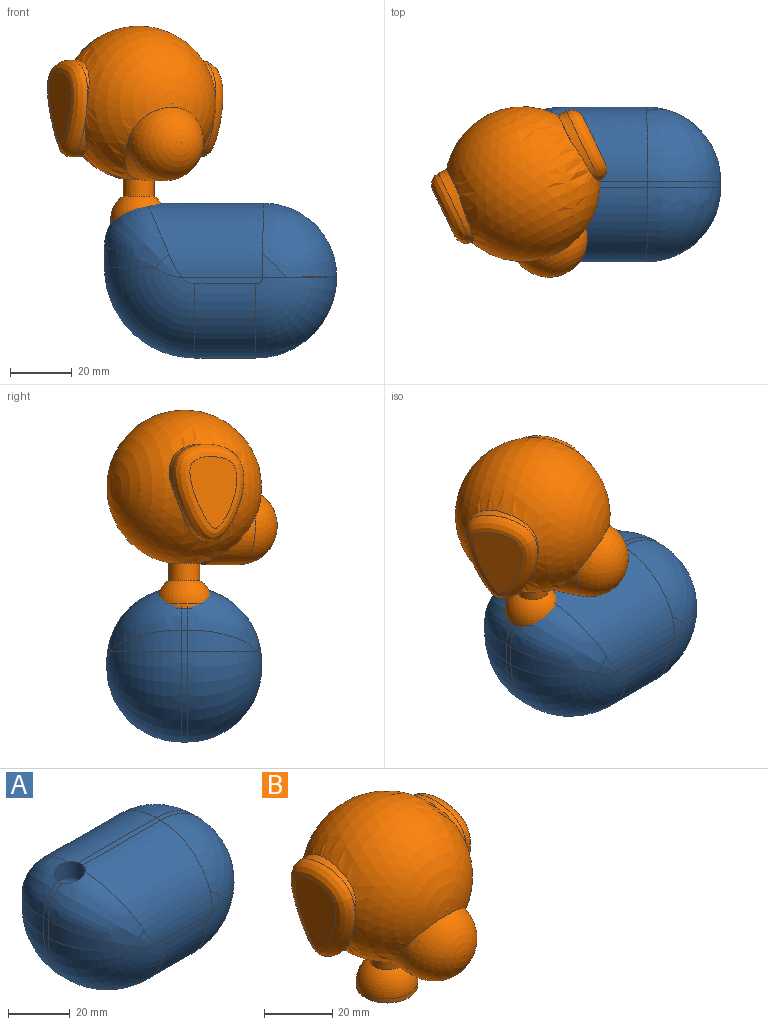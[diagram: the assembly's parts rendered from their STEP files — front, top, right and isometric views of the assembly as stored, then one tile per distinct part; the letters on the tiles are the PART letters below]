
ASSEMBLY  parts=2 mates=1
PART A: 33 faces, bbox 75x50x50 mm
  f0: cylinder r=13.85mm len=11.48mm, axis (0,1,0), area 26.9mm2, adj f1,f3,f6,f30
  f1: bspline ~24.89x21.37mm, area 506.7mm2, adj f0,f2,f14,f15,f30
  f2: cylinder r=24mm len=37.4mm, axis (-1,0,0), area 1239.4mm2, adj f1,f5,f13,f15,f17,f20,f30
  f3: bspline ~24.89x21.37mm, area 506.7mm2, adj f0,f4,f22,f23,f30
  f4: cylinder r=24mm len=37.4mm, axis (1,0,0), area 1239.4mm2, adj f3,f5,f12,f23,f25,f27,f30
  f5: plane 35.43x2mm, normal (0,0,1), area 70.7mm2, adj f2,f4,f11,f30
  f6: plane 6.95x2mm, normal (-1,0,0), area 13.9mm2, adj f0,f7,f14,f22
  f7: cylinder r=29.21mm len=29.21mm, axis (0,1,0), area 91.8mm2, adj f6,f8,f16,f24
  f8: plane 19.69x2mm, normal (0,0,-1), area 39.4mm2, adj f7,f9,f18,f26
  f9: cylinder r=26.11mm len=26.11mm, axis (0,1,0), area 82mm2, adj f8,f10,f21,f29
  f10: plane 2x0.22mm, normal (1,0,0), area 0.4mm2, adj f9,f11,f19,f28
  f11: cylinder r=23.67mm len=23.67mm, axis (0,1,0), area 74.4mm2, adj f5,f10,f17,f25
  f12: plane 25.89x2mm, normal (0,-1,0), area 48.4mm2, adj f4,f24,f26,f29
  f13: plane 25.89x2mm, normal (0,1,0), area 48.4mm2, adj f2,f16,f18,f21
  f14: cylinder r=24mm len=22.77mm, axis (0,0,-1), area 104.1mm2, adj f1,f6,f16
  f15: bspline ~11.03x10.01mm, area 19.7mm2, adj f1,f2,f16
  f16: torus R=5.21mm, axis (0,-1,0), area 1193.2mm2, adj f7,f13,f14,f15,f18
  f17: bspline ~25.54x23.92mm, area 861.5mm2, adj f2,f11,f19,f20
  f18: cylinder r=24mm len=24mm, axis (1,0,0), area 742.2mm2, adj f8,f13,f16,f21
  f19: cylinder r=24mm len=22.7mm, axis (0,0,1), area 3.3mm2, adj f10,f17,f21
  f20: bspline ~13.33x13.26mm, area 22.1mm2, adj f2,f17,f21
  f21: torus R=2.11mm, axis (0,-1,0), area 1028.6mm2, adj f9,f13,f18,f19,f20
  f22: cylinder r=24mm len=22.77mm, axis (0,0,1), area 104.1mm2, adj f3,f6,f24
  f23: bspline ~11.03x10.01mm, area 19.7mm2, adj f3,f4,f24
  f24: torus R=5.21mm, axis (0,-1,0), area 1193.2mm2, adj f7,f12,f22,f23,f26
  f25: bspline ~25.54x23.92mm, area 861.5mm2, adj f4,f11,f27,f28
  f26: cylinder r=24mm len=24mm, axis (-1,0,0), area 742.2mm2, adj f8,f12,f24,f29
  f27: bspline ~13.33x13.26mm, area 22.1mm2, adj f4,f25,f29
  f28: cylinder r=24mm len=22.7mm, axis (0,0,-1), area 3.3mm2, adj f10,f25,f29
  f29: torus R=2.11mm, axis (0,-1,0), area 1028.6mm2, adj f9,f12,f26,f27,f28
  f30: cylinder r=5mm len=10mm, axis (0,0,-1), area 180.1mm2, adj f0,f1,f2,f3,f4,f5,f31
  f31: plane 18x18mm, normal (0,0,-1), area 175.9mm2, adj f30,f32
  f32: sphere r=9mm, area 508.9mm2, adj f31
PART B: 19 faces, bbox 58.2x61.2x77.2 mm
  f0: sphere r=25mm, area 6004.2mm2, adj f1,f2,f3,f4,f9,f10,f12,f13
  f1: cylinder r=12.5mm len=25mm, axis (0,1,0), area 368.3mm2, adj f0,f2,f4
  f2: plane 13.44x1.96mm, normal (0,1,0), area 9.2mm2, adj f0,f1
  f3: cylinder r=5mm len=10mm, axis (0,0,1), area 172.9mm2, adj f0,f7
  f4: sphere r=12.5mm, area 981.7mm2, adj f0,f1
  f5: cylinder r=9mm len=18mm, axis (0,0,1), area 85.8mm2, adj f7,f8
  f6: plane 0x0mm, normal (0,0,-1), area 0mm2, adj f8
  f7: torus R=0mm, axis (0,0,1), area 423.2mm2, adj f3,f5
  f8: torus R=0mm, axis (0,0,1), area 508.9mm2, adj f5,f6
  f9: plane 15.87x13.77mm, normal (-1,0,0), area 17.5mm2, adj f0,f10
  f10: extruded ~31.27x24.77mm, area 195mm2, adj f0,f9,f12,f13
  f11: plane 23.33x16.81mm, normal (1,0,0), area 281.7mm2, adj f13
  f12: plane 12x5.51mm, normal (-1,0,0), area 19.1mm2, adj f0,f10
  f13: bspline ~31.34x24.82mm, area 488.5mm2, adj f0,f10,f11
  f14: plane 12x5.51mm, normal (1,0,0), area 19.1mm2, adj f0,f15
  f15: extruded ~31.27x24.77mm, area 195mm2, adj f0,f14,f17,f18
  f16: plane 23.33x16.81mm, normal (-1,0,0), area 281.7mm2, adj f18
  f17: plane 15.87x13.77mm, normal (1,0,0), area 17.5mm2, adj f0,f15
  f18: bspline ~31.34x24.81mm, area 488.5mm2, adj f0,f15,f16
PLACE A t=(-5.15,0.77,-6.76)mm fixed
PLACE B rot(axis=(0,0,1),25.7deg) t=(-25.79,0.77,57.24)mm
MATE revolute A.f30 <-> B.f5  axis (0,0,1) through (-25.79,0.77,18.24)mm
